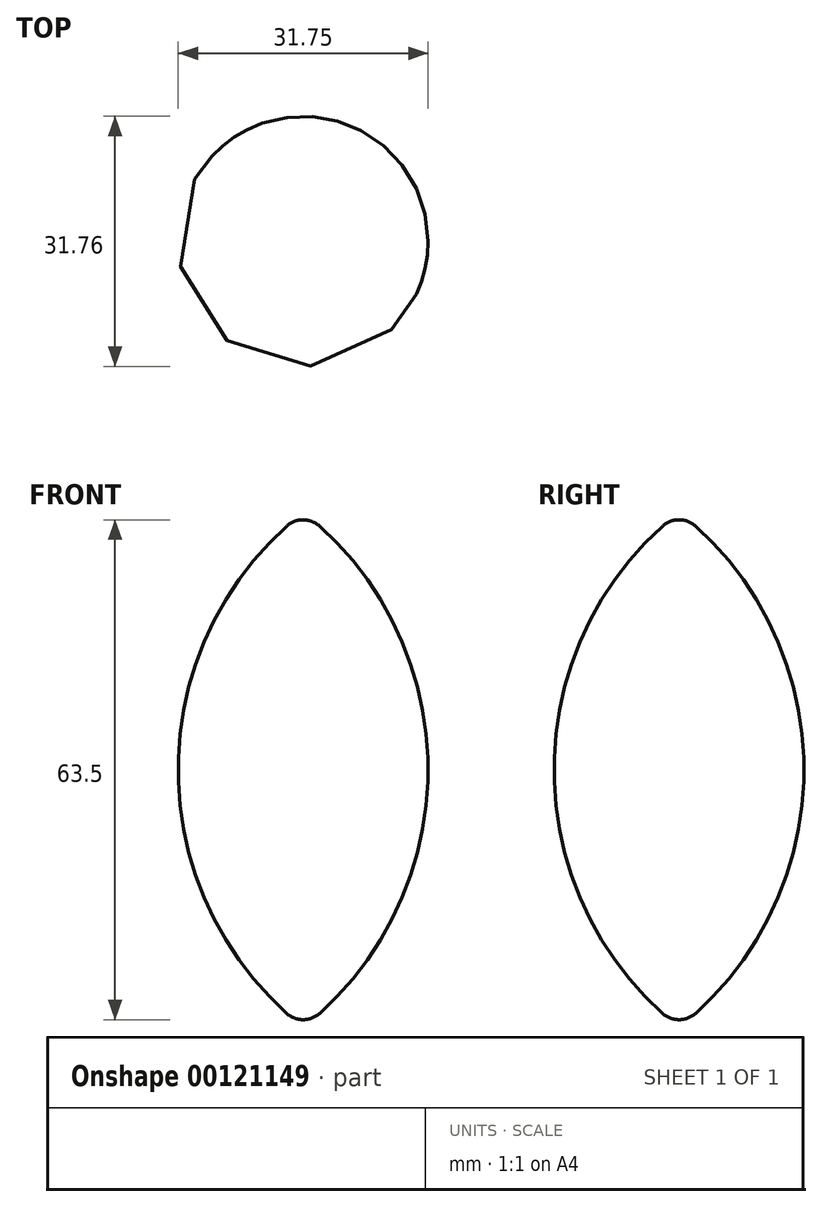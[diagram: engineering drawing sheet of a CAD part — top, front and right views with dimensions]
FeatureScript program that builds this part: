
annotation { "Feature Type Name" : "Feature", "Feature Type Description" : "" }
export const myFeature = defineFeature(function(context is Context, id is Id, definition is map)
    precondition{}
    {
        {
            var Q0;
            Q0=qCreatedBy(makeId("Front.planeOp"),FACE);
            var sketch = newSketch(context, id + "F0", { "sketchPlane" : qUnion([Q0])});
            skLineSegment(sketch, "E0", {"start": v(0, 31.75) * mm, "end": v(0, -31.75) * mm});
            skLineSegment(sketch, "E1", {"start": v(0, -31.75) * mm, "end": v(0, 49.35) * mm, "construction": true});
            skLineSegment(sketch, "E2", {"start": v(0, 0) * mm, "end": v(15.88, 0) * mm, "construction": true});
            skArc(sketch, "E3", {"start": v(2.13, -30.93) * mm, "mid": v(15.88, 0) * mm, "end": v(2.13, 30.93) * mm});
            skArc(sketch, "E4", {"start": v(2.13, 30.93) * mm, "mid": v(1.14, 31.54) * mm, "end": v(0, 31.75) * mm});
            skArc(sketch, "E5", {"start": v(2.13, -30.93) * mm, "mid": v(1.14, -31.54) * mm, "end": v(0, -31.75) * mm});
            skSolve(sketch);
        }
        {
            var Q0;
            Q0=makeQuery(id+"F0.imprint","IMPRINT",FACE,{"disambiguationData":[TD([[makeQuery(id+"F0.imprint","IMPRINT",EDGE,{"derivedFrom":sQuery(id+"F0.wireOp",EDGE,"E0")}),1.0]])]});
            var Q1;
            Q1=sQuery(id+"F0.wireOp",EDGE,"E0");
            revolve(context, id + "F1", {"entities" : qUnion([Q0]), "axis" : qUnion([Q1]), "revolveType" : RevolveType.FULL});
        }
    });
